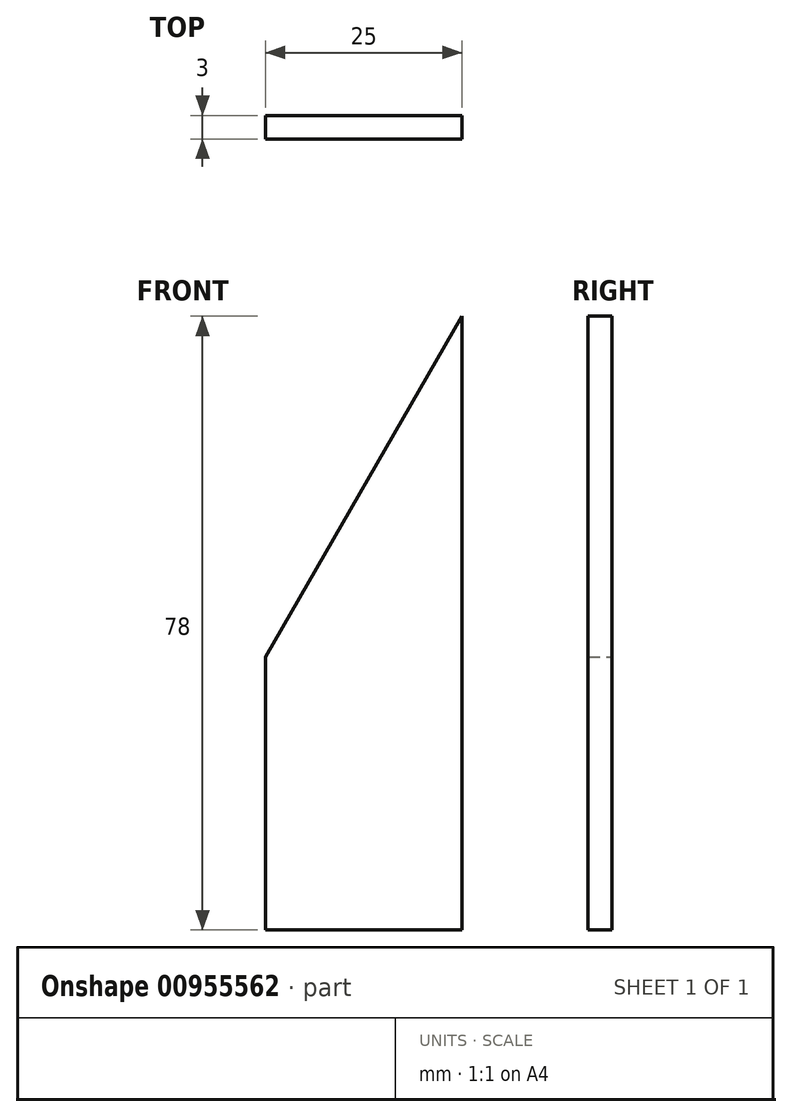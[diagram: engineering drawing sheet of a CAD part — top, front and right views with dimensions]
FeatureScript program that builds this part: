
annotation { "Feature Type Name" : "Feature", "Feature Type Description" : "" }
export const myFeature = defineFeature(function(context is Context, id is Id, definition is map)
    precondition{}
    {
        {
            var Q0;
            Q0=qCreatedBy(makeId("Front.planeOp"),FACE);
            var sketch = newSketch(context, id + "F0", { "sketchPlane" : qUnion([Q0])});
            skLineSegment(sketch, "E0.bottom", {"start": v(12.5, -39) * mm, "end": v(-12.5, -39) * mm});
            skLineSegment(sketch, "E0.left", {"start": v(12.5, -39) * mm, "end": v(12.5, 39) * mm});
            skLineSegment(sketch, "E0.right", {"start": v(-12.5, -39) * mm, "end": v(-12.5, -4.3) * mm});
            skPoint(sketch, "E0.middle", {"position": v(0, 0) * mm});
            skLineSegment(sketch, "E1", {"start": v(12.5, 39) * mm, "end": v(-12.5, -4.3) * mm});
            skSolve(sketch);
        }
        {
            var Q0;
            Q0 = qSketchRegion(id + "F0", true);
            extrude(context, id + "F1", {"entities" : qUnion([Q0]), "depth" : 3 * mm, "offsetDistance" : 25 * mm});
        }
    });
